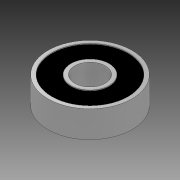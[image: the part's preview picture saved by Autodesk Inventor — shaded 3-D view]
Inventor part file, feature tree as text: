
AUTODESK INVENTOR PART (.ipt)
format: ipt  version: 2022 (Build 260153000, 153)  size: 131,072 bytes
history: native  units: mm
features: revolve x1, sketch x1
ambient origin geometry x8: Origin, YZ Plane, XZ Plane, XY Plane, X Axis, Y Axis, Z Axis, Center Point
bodies: Solid1 (feature_tree)
feature tree (2):
  revolve  "Revolution1"  [1 undecoded]
  sketch  "Sketch1"  dims[d0=4.0mm d2=7.0mm d5=11.0mm d6=0.2mm d7=1.0mm d8=90.0deg]
note: 1 required parameter value undecoded (feature->parameter linkage not recoverable at this tier; creation-order binding heuristic only, values carry confidence <= 0.55)
